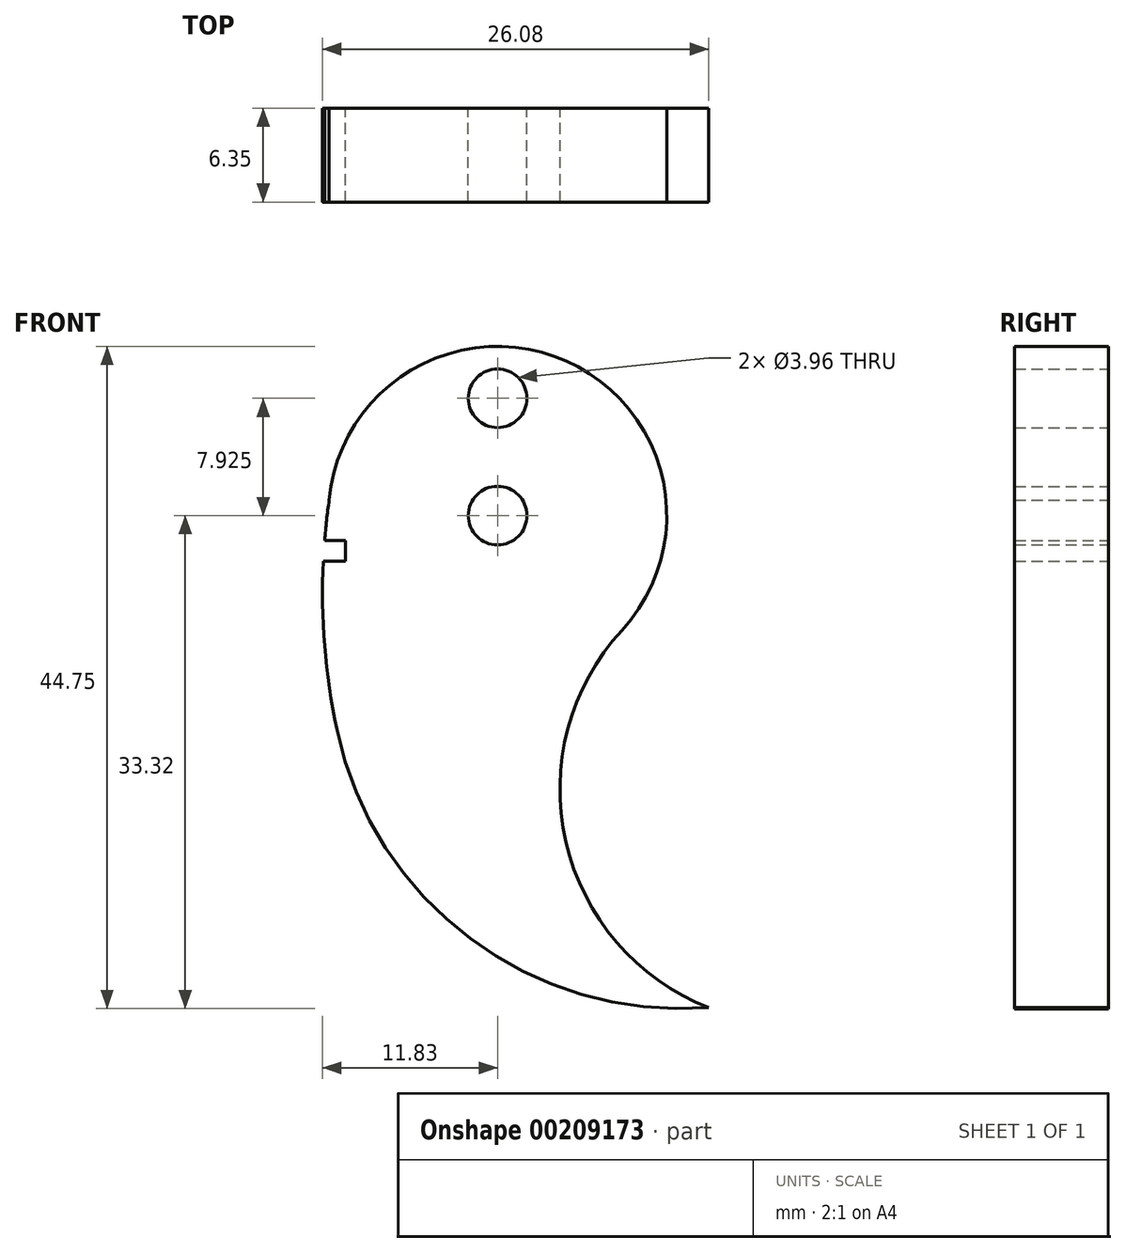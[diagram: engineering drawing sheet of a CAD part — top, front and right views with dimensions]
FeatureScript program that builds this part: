
annotation { "Feature Type Name" : "Feature", "Feature Type Description" : "" }
export const myFeature = defineFeature(function(context is Context, id is Id, definition is map)
    precondition{}
    {
        {
            var Q0;
            Q0=qCreatedBy(makeId("Front.planeOp"),FACE);
            var sketch = newSketch(context, id + "F0", { "sketchPlane" : qUnion([Q0])});
            skCircle(sketch, "E0", {"center": v(0, 0) * mm, "radius": 1.98 * mm});
            skCircle(sketch, "E1", {"center": v(0, 7.92) * mm, "radius": 1.98 * mm});
            skArc(sketch, "E2", {"start": v(8.41, -7.74) * mm, "mid": v(4.64, 10.45) * mm, "end": v(-11.38, 1.04) * mm});
            skArc(sketch, "E3", {"start": v(-11.14, 2.57) * mm, "mid": v(-11.46, 0.45) * mm, "end": v(-11.69, -1.68) * mm});
            skArc(sketch, "E4", {"start": v(-10.86, -14.46) * mm, "mid": v(-1.84, -28.58) * mm, "end": v(14.25, -33.25) * mm});
            skArc(sketch, "E5", {"start": v(14.25, -33.25) * mm, "mid": v(4.62, -22.04) * mm, "end": v(8.41, -7.74) * mm});
            skLineSegment(sketch, "E6", {"start": v(-11.69, -1.68) * mm, "end": v(-10.29, -1.68) * mm});
            skLineSegment(sketch, "E7", {"start": v(-10.29, -1.68) * mm, "end": v(-10.29, -3.08) * mm});
            skLineSegment(sketch, "E8", {"start": v(-10.29, -3.08) * mm, "end": v(-11.78, -3.08) * mm});
            skArc(sketch, "E9.trimOffspring", {"start": v(-11.78, -3.08) * mm, "mid": v(-11.55, -10.18) * mm, "end": v(-10.2, -17.15) * mm});
            skSolve(sketch);
        }
        {
            var Q0;
            Q0 = qSketchRegion(id + "F0", true);
            extrude(context, id + "F1", {"entities" : qUnion([Q0]), "depth" : 6.35 * mm});
        }
    });
